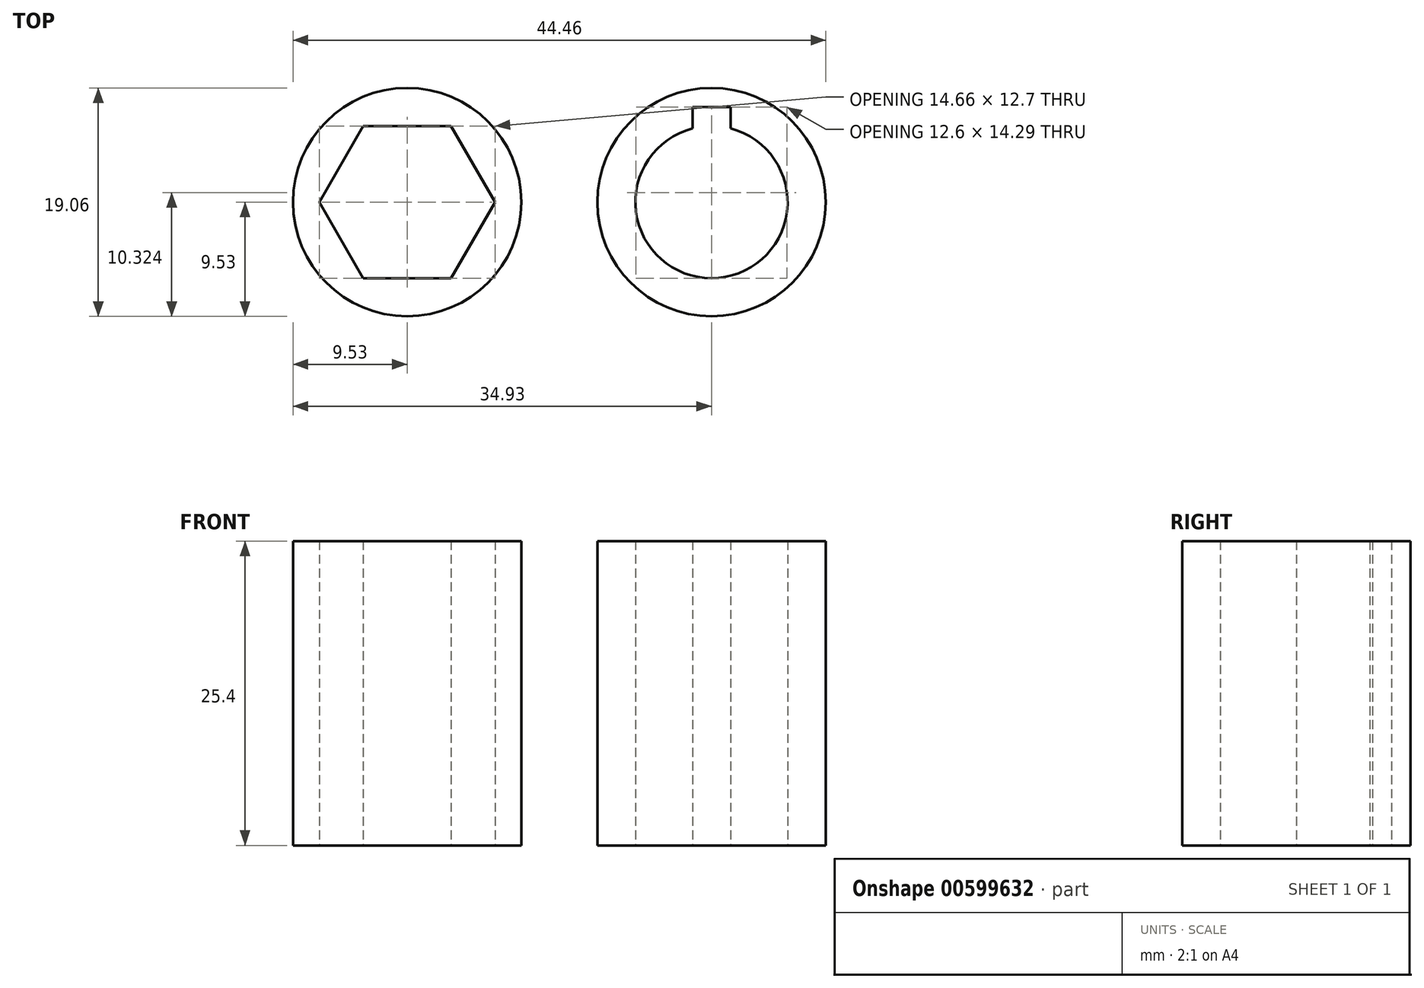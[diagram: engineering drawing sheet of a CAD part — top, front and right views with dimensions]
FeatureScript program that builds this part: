
annotation { "Feature Type Name" : "Feature", "Feature Type Description" : "" }
export const myFeature = defineFeature(function(context is Context, id is Id, definition is map)
    precondition{}
    {
        {
            var Q0;
            Q0=qCreatedBy(makeId("Top.planeOp"),FACE);
            var sketch = newSketch(context, id + "F0", { "sketchPlane" : qUnion([Q0])});
            skCircle(sketch, "E0", {"center": v(0, 0) * mm, "radius": 9.53 * mm});
            skCircle(sketch, "E1.cCircle", {"center": v(0, 0) * mm, "radius": 6.35 * mm, "construction": true});
            skLineSegment(sketch, "E1.0", {"start": v(7.33, 0) * mm, "end": v(3.67, -6.35) * mm});
            skLineSegment(sketch, "E1.1", {"start": v(3.67, -6.35) * mm, "end": v(-3.67, -6.35) * mm});
            skLineSegment(sketch, "E1.2", {"start": v(-3.67, -6.35) * mm, "end": v(-7.33, 0) * mm});
            skLineSegment(sketch, "E1.3", {"start": v(-7.33, 0) * mm, "end": v(-3.67, 6.35) * mm});
            skLineSegment(sketch, "E1.4", {"start": v(-3.67, 6.35) * mm, "end": v(3.67, 6.35) * mm});
            skLineSegment(sketch, "E1.5", {"start": v(3.67, 6.35) * mm, "end": v(7.33, 0) * mm});
            skPoint(sketch, "E1.0.midPoint", {"position": v(5.5, -3.18) * mm});
            skCircle(sketch, "E2", {"center": v(25.4, 0) * mm, "radius": 9.53 * mm});
            skCircle(sketch, "E3", {"center": v(25.4, 0) * mm, "radius": 6.35 * mm});
            skLineSegment(sketch, "E4.bottom", {"start": v(26.99, 4.76) * mm, "end": v(23.81, 4.76) * mm});
            skLineSegment(sketch, "E4.top", {"start": v(26.99, 7.94) * mm, "end": v(23.81, 7.94) * mm});
            skLineSegment(sketch, "E4.left", {"start": v(26.99, 4.76) * mm, "end": v(26.99, 7.94) * mm});
            skLineSegment(sketch, "E4.right", {"start": v(23.81, 4.76) * mm, "end": v(23.81, 7.94) * mm});
            skPoint(sketch, "E4.middle", {"position": v(25.4, 6.35) * mm});
            skSolve(sketch);
        }
        {
            var Q0;
            Q0=makeQuery(id+"F0.imprint","IMPRINT",FACE,{"disambiguationData":[TD([[makeQuery(id+"F0.imprint","IMPRINT",EDGE,{"derivedFrom":sQuery(id+"F0.wireOp",EDGE,"E2")}),1.0]])]});
            var Q1;
            Q1=makeQuery(id+"F0.imprint","IMPRINT",FACE,{"disambiguationData":[TD([[makeQuery(id+"F0.imprint","IMPRINT",EDGE,{"derivedFrom":sQuery(id+"F0.wireOp",EDGE,"E0")}),1.0]])]});
            extrude(context, id + "F1", {"entities" : qUnion([Q0, Q1]), "depth" : 25.4 * mm, "offsetDistance" : 25.4 * mm});
        }
    });
